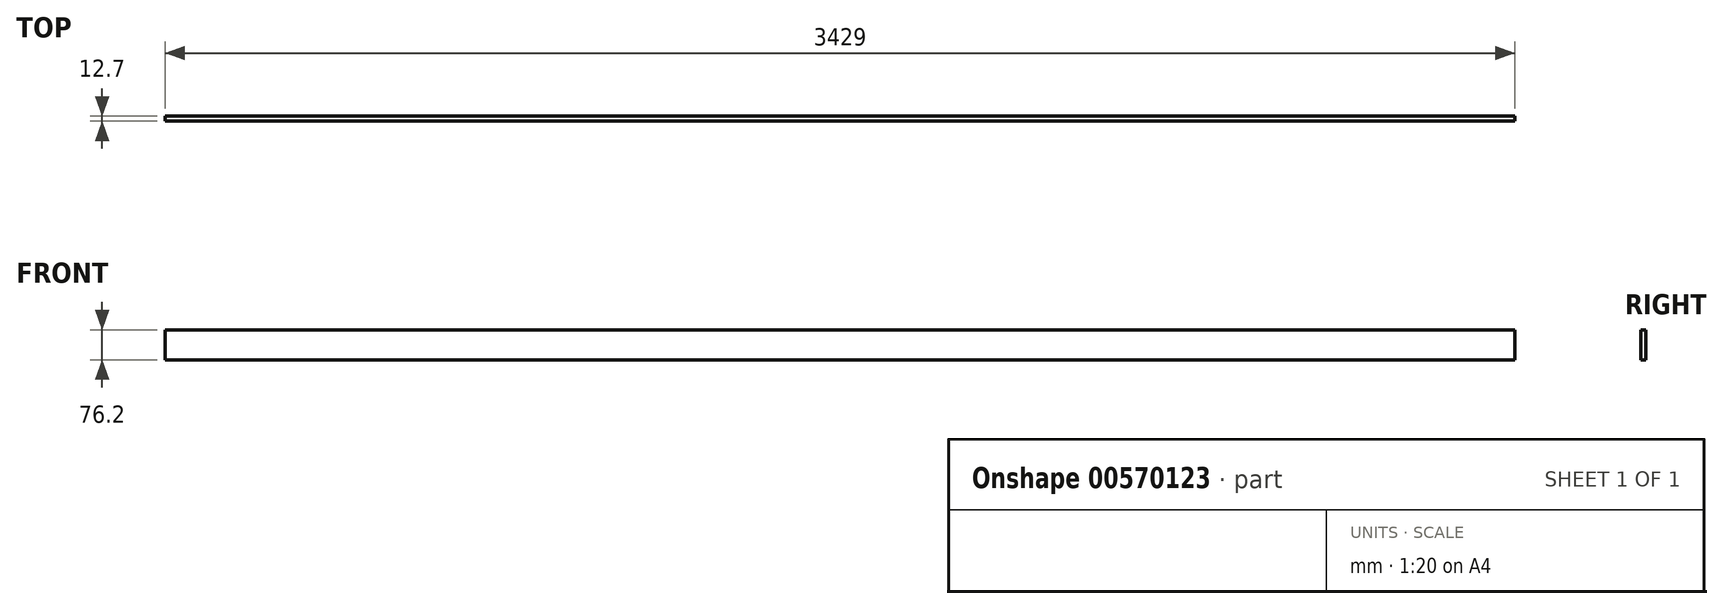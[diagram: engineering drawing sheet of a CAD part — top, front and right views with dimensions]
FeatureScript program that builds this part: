
annotation { "Feature Type Name" : "Feature", "Feature Type Description" : "" }
export const myFeature = defineFeature(function(context is Context, id is Id, definition is map)
    precondition{}
    {
        {
            var Q0;
            Q0=qCreatedBy(makeId("Right.planeOp"),FACE);
            var sketch = newSketch(context, id + "F0", { "sketchPlane" : qUnion([Q0])});
            skLineSegment(sketch, "E0.bottom", {"start": v(6.35, 38.1) * mm, "end": v(-6.35, 38.1) * mm});
            skLineSegment(sketch, "E0.top", {"start": v(6.35, -38.1) * mm, "end": v(-6.35, -38.1) * mm});
            skLineSegment(sketch, "E0.left", {"start": v(6.35, 38.1) * mm, "end": v(6.35, -38.1) * mm});
            skLineSegment(sketch, "E0.right", {"start": v(-6.35, 38.1) * mm, "end": v(-6.35, -38.1) * mm});
            skPoint(sketch, "E0.middle", {"position": v(0, 0) * mm});
            skSolve(sketch);
        }
        {
            var Q0;
            Q0=makeQuery(id+"F0.imprint","IMPRINT",FACE,{"disambiguationData":[TD([[makeQuery(id+"F0.imprint","IMPRINT",EDGE,{"derivedFrom":sQuery(id+"F0.wireOp",EDGE,"E0.bottom")}),1.0]])]});
            extrude(context, id + "F1", {"entities" : qUnion([Q0]), "endBound" : BoundingType.SYMMETRIC, "depth" : 3352.8 * mm + 76.2 * mm, "offsetDistance" : 25.4 * mm});
        }
    });
